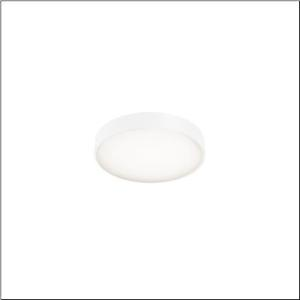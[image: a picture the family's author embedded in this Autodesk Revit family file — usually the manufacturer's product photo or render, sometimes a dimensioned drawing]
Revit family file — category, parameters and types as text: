
# Revit family: round_21_s_51mr34fd0421w
name_source: partatom
category: Lighting Fixtures
units: mm (PartAtom-declared; Revit-internal decimal feet)

## family parameters
Cut with Voids When Loaded = No
Host = Face
Light Source = No
Part Type = Normal
Room Calculation Point = No
Round Connector Dimension = Use Diameter
Shared = No

## types (1)
- Round 21 S (1 x LED, 3910 lm, 30.3 W, 4000K)
    Apparent Load = 30 VA
    CIE Flux Codes = 49 80 96 100 100
    Color Rendering = 80
    Color Temperature = 4000K
    Default Elevation = 1800 mm
    Description = Round 21 S, wall and ceiling luminaire, primary optical cover: cover, of PMMA, opal, light emission: direct distribution, primary light characteristic: symmetric, installation type: suspended mounting, surface-mounted, LED, rated luminous flux: 3.900lm, luminous efficacy: 129lm/W, light colour: 840, colour temperature: 4000K, control gear: DALI 2, with terminal, 5-pole, mains connection: 230V, AC, 50/60Hz, rated input power: 30.3W, housing, of aluminium, coated, white, diameter: 400mm, height: 62mm, protection rating (complete): IP40, insulation class (complete): insulation class I (protective earthing), certification: CE, impact resistance: IK04, permissible operating ambient temperature: -10..+35°C, packaging unit: 1 piece
    Height = 87 mm
    Lamp = 1 x LED
    Lamp Light Flux = 3910 lm
    Lamp Power = 30.3 W
    Lamp count = 1
    Length = 400 mm
    Luminous efficacy = 129 lm/W
    Manufacturer = Siteco
    ModVariant = No
    Model = 51MR34FD0421W
    Mounting Place = Wall
    Mounting Type = Surface mounted
    Number of Poles = 1
    OnlyDefault = Yes
    Power Factor = 1
    Product Name = Round 21 S
    Product group = wall and ceiling luminaire
    ProductGroupID = 2001
    Protection Class = Protection class I
    Protection Degree = IP 40
    RLX_Detail_Level = 1
    RLX_Emergency_Light_Flux = 0 lm
    RLX_Emergency_Type = 0
    RLX_Emergency_Type_DB = No
    RlxData = <blob elided: 9509 chars, md5=7a9f5b3e>
    Socket = socket
    Standby Power = 0 W
    System Light Flux = 3910 lm
    System Power = 30 W
    Type Comments = Product without accessories
    Type Image = l_1258307.jpg
    URL = http://relux.com
    VarID = ---
    Voltage = 0 V
    Weight = 0.00 kg
    Width = 0 mm  [stored 0 ft]

note: [stored X ft] marks values corroborated as IEEE doubles in the binary element streams (Revit-internal decimal feet)

## geometry (parser evidence)
native form markers: Sweep x9
no freeform markers — native parametric forms only
